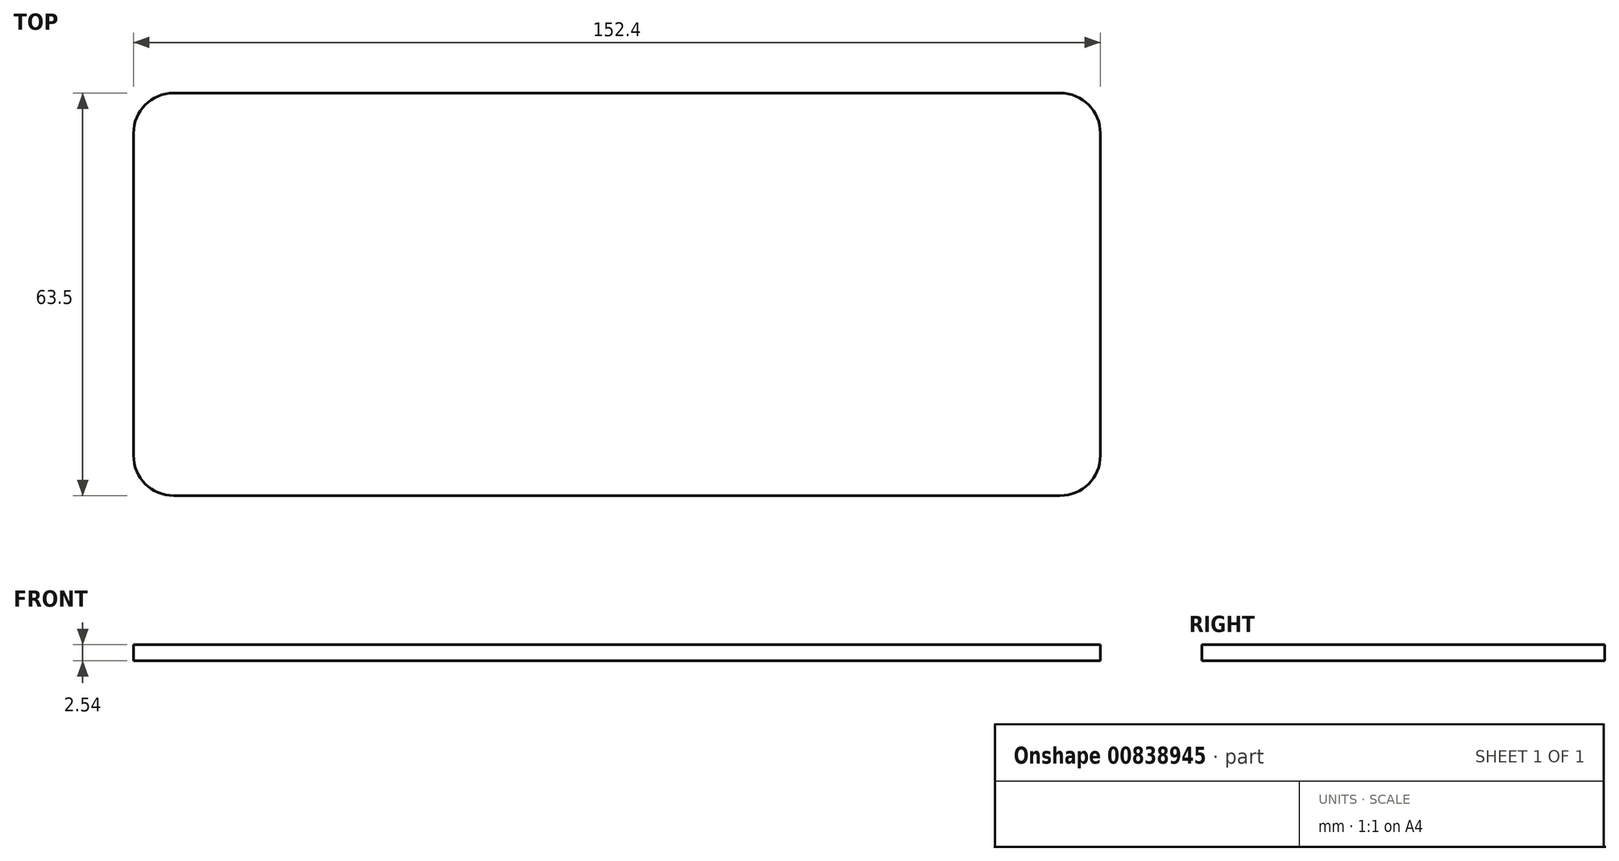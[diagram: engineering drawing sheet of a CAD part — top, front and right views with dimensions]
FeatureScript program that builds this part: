
annotation { "Feature Type Name" : "Feature", "Feature Type Description" : "" }
export const myFeature = defineFeature(function(context is Context, id is Id, definition is map)
    precondition{}
    {
        {
            var Q0;
            Q0=qCreatedBy(makeId("Top.planeOp"),FACE);
            var sketch = newSketch(context, id + "F0", { "sketchPlane" : qUnion([Q0])});
            skLineSegment(sketch, "E0.bottom", {"start": v(-70.75, 0.08) * mm, "end": v(68.95, 0.08) * mm});
            skLineSegment(sketch, "E0.top", {"start": v(-70.75, -63.42) * mm, "end": v(68.95, -63.42) * mm});
            skLineSegment(sketch, "E0.left", {"start": v(-77.1, -6.27) * mm, "end": v(-77.1, -57.07) * mm});
            skLineSegment(sketch, "E0.right", {"start": v(75.3, -6.27) * mm, "end": v(75.3, -57.07) * mm});
            skPoint(sketch, "E1.visualSharp", {"position": v(-77.1, 0.08) * mm});
            skArc(sketch, "E1.filletArc", {"start": v(-70.75, 0.08) * mm, "mid": v(-75.24, -1.78) * mm, "end": v(-77.1, -6.27) * mm});
            skPoint(sketch, "E2.visualSharp", {"position": v(75.3, 0.08) * mm});
            skArc(sketch, "E2.filletArc", {"start": v(75.3, -6.27) * mm, "mid": v(73.44, -1.78) * mm, "end": v(68.95, 0.08) * mm});
            skPoint(sketch, "E3.visualSharp", {"position": v(75.3, -63.42) * mm});
            skArc(sketch, "E3.filletArc", {"start": v(68.95, -63.42) * mm, "mid": v(73.44, -61.56) * mm, "end": v(75.3, -57.07) * mm});
            skPoint(sketch, "E4.visualSharp", {"position": v(-77.1, -63.42) * mm});
            skArc(sketch, "E4.filletArc", {"start": v(-77.1, -57.07) * mm, "mid": v(-75.24, -61.56) * mm, "end": v(-70.75, -63.42) * mm});
            skSolve(sketch);
        }
        {
            var Q0;
            Q0 = qSketchRegion(id + "F0", true);
            extrude(context, id + "F1", {"entities" : qUnion([Q0]), "depth" : 2.54 * mm, "offsetDistance" : 25.4 * mm});
        }
    });
